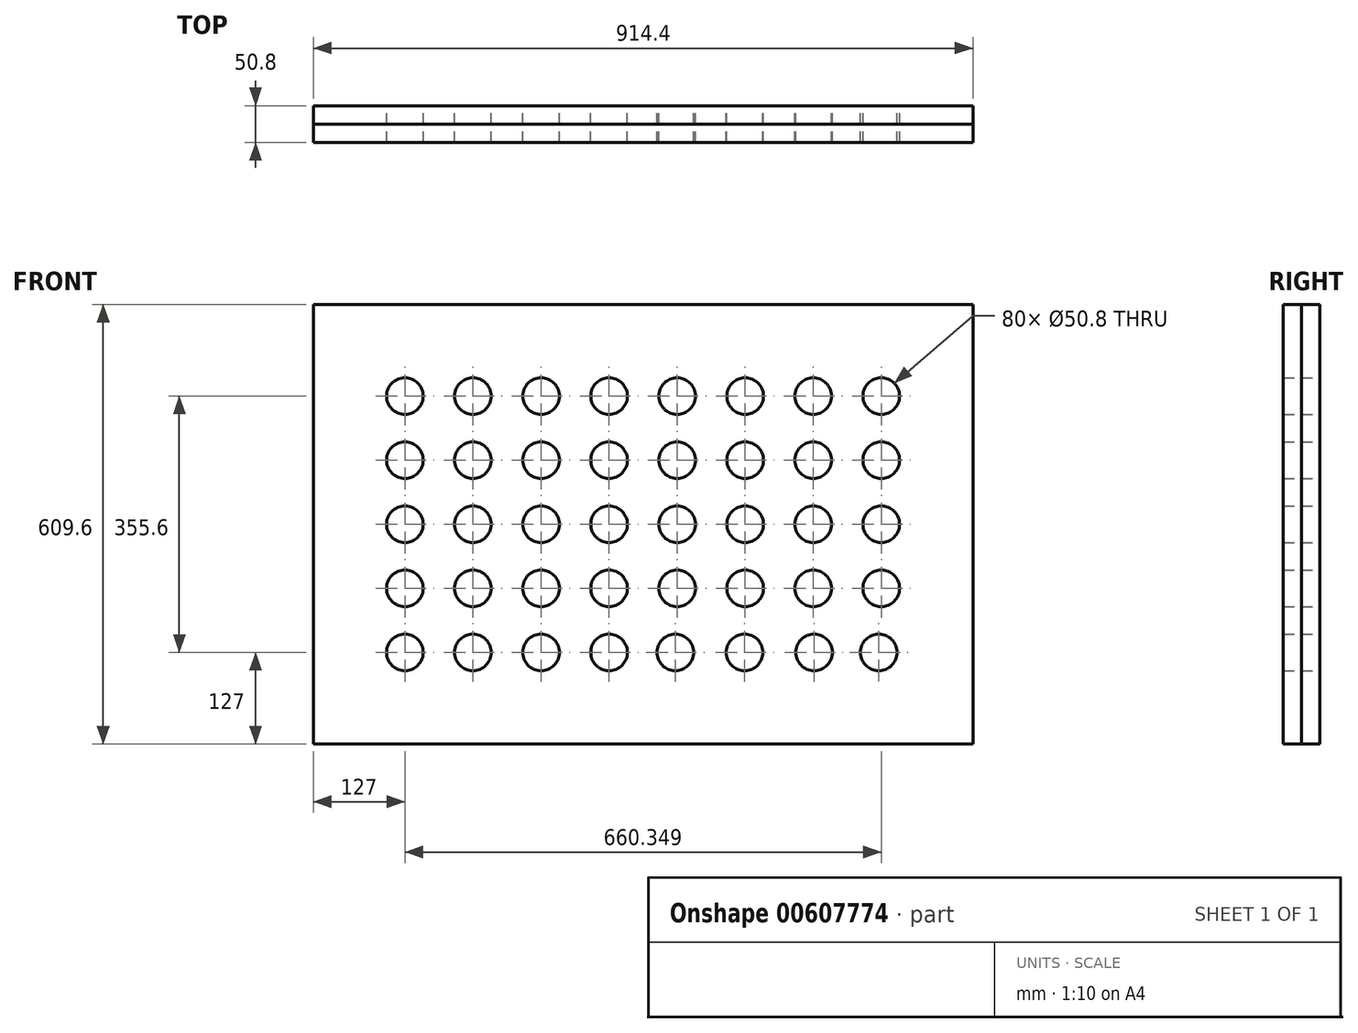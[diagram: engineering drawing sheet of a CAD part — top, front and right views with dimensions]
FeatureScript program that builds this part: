
annotation { "Feature Type Name" : "Feature", "Feature Type Description" : "" }
export const myFeature = defineFeature(function(context is Context, id is Id, definition is map)
    precondition{}
    {
        {
            var Q0;
            Q0=qCreatedBy(makeId("Front.planeOp"),FACE);
            var sketch = newSketch(context, id + "F0", { "sketchPlane" : qUnion([Q0])});
            skLineSegment(sketch, "E0.bottom", {"start": v(0, 0) * mm, "end": v(-914.4, 0) * mm});
            skLineSegment(sketch, "E0.top", {"start": v(0, 609.6) * mm, "end": v(-914.4, 609.6) * mm});
            skLineSegment(sketch, "E0.left", {"start": v(0, 0) * mm, "end": v(0, 609.6) * mm});
            skLineSegment(sketch, "E0.right", {"start": v(-914.4, 0) * mm, "end": v(-914.4, 609.6) * mm});
            skCircle(sketch, "E1", {"center": v(-787.4, 482.6) * mm, "radius": 25.4 * mm});
            skCircle(sketch, "E2", {"center": v(-787.4, 393.7) * mm, "radius": 25.4 * mm});
            skCircle(sketch, "E3", {"center": v(-787.4, 304.8) * mm, "radius": 25.4 * mm});
            skCircle(sketch, "E4", {"center": v(-787.4, 215.9) * mm, "radius": 25.4 * mm});
            skCircle(sketch, "E5", {"center": v(-787.4, 127) * mm, "radius": 25.4 * mm});
            skCircle(sketch, "E6", {"center": v(-693.06, 482.6) * mm, "radius": 25.4 * mm});
            skCircle(sketch, "E7", {"center": v(-598.73, 482.6) * mm, "radius": 25.4 * mm});
            skCircle(sketch, "E8", {"center": v(-504.4, 482.6) * mm, "radius": 25.4 * mm});
            skCircle(sketch, "E9", {"center": v(-410.06, 482.6) * mm, "radius": 25.4 * mm});
            skCircle(sketch, "E10", {"center": v(-315.72, 482.6) * mm, "radius": 25.4 * mm});
            skCircle(sketch, "E11", {"center": v(-221.39, 482.6) * mm, "radius": 25.4 * mm});
            skCircle(sketch, "E12", {"center": v(-127.05, 482.6) * mm, "radius": 25.4 * mm});
            skCircle(sketch, "E13", {"center": v(-693.06, 393.7) * mm, "radius": 25.4 * mm});
            skCircle(sketch, "E14", {"center": v(-598.73, 393.7) * mm, "radius": 25.4 * mm});
            skCircle(sketch, "E15", {"center": v(-504.4, 393.7) * mm, "radius": 25.4 * mm});
            skCircle(sketch, "E16", {"center": v(-410.06, 393.7) * mm, "radius": 25.4 * mm});
            skCircle(sketch, "E17", {"center": v(-315.72, 393.7) * mm, "radius": 25.4 * mm});
            skCircle(sketch, "E18", {"center": v(-221.39, 393.7) * mm, "radius": 25.4 * mm});
            skCircle(sketch, "E19", {"center": v(-127.05, 393.7) * mm, "radius": 25.4 * mm});
            skCircle(sketch, "E20", {"center": v(-693.06, 304.8) * mm, "radius": 25.4 * mm});
            skCircle(sketch, "E21", {"center": v(-598.73, 304.8) * mm, "radius": 25.4 * mm});
            skCircle(sketch, "E22", {"center": v(-504.4, 304.8) * mm, "radius": 25.4 * mm});
            skCircle(sketch, "E23", {"center": v(-410.06, 304.8) * mm, "radius": 25.4 * mm});
            skCircle(sketch, "E24", {"center": v(-315.72, 304.8) * mm, "radius": 25.4 * mm});
            skCircle(sketch, "E25", {"center": v(-221.39, 304.8) * mm, "radius": 25.4 * mm});
            skCircle(sketch, "E26", {"center": v(-127.05, 304.8) * mm, "radius": 25.4 * mm});
            skCircle(sketch, "E27", {"center": v(-693.06, 215.9) * mm, "radius": 25.4 * mm});
            skCircle(sketch, "E28", {"center": v(-598.73, 215.9) * mm, "radius": 25.4 * mm});
            skCircle(sketch, "E29", {"center": v(-504.4, 215.9) * mm, "radius": 25.4 * mm});
            skCircle(sketch, "E30", {"center": v(-410.06, 215.9) * mm, "radius": 25.4 * mm});
            skCircle(sketch, "E31", {"center": v(-315.72, 215.9) * mm, "radius": 25.4 * mm});
            skCircle(sketch, "E32", {"center": v(-221.39, 215.9) * mm, "radius": 25.4 * mm});
            skCircle(sketch, "E33", {"center": v(-127.05, 215.9) * mm, "radius": 25.4 * mm});
            skCircle(sketch, "E34", {"center": v(-693.06, 127) * mm, "radius": 25.4 * mm});
            skCircle(sketch, "E35", {"center": v(-598.73, 127) * mm, "radius": 25.4 * mm});
            skCircle(sketch, "E36", {"center": v(-504.4, 127) * mm, "radius": 25.4 * mm});
            skCircle(sketch, "E37", {"center": v(-412.6, 127.04) * mm, "radius": 25.4 * mm});
            skCircle(sketch, "E38", {"center": v(-316.44, 127) * mm, "radius": 25.4 * mm});
            skCircle(sketch, "E39", {"center": v(-220.22, 127) * mm, "radius": 25.4 * mm});
            skCircle(sketch, "E40", {"center": v(-130.5, 127.07) * mm, "radius": 25.4 * mm});
            skSolve(sketch);
        }
        {
            var Q0;
            Q0 = qSketchRegion(id + "F0", true);
            extrude(context, id + "F1", {"entities" : qUnion([Q0]), "depth" : 25.4 * mm, "offsetDistance" : 25.4 * mm});
        }
        {
            var Q0;
            Q0=makeQuery(id+"F1.opExtrude","CAP_FACE",FACE,{"disambiguationData":[OSD([sQuery(id+"F0.wireOp",EDGE,"E0.bottom"),sQuery(id+"F0.wireOp",EDGE,"E0.top"),sQuery(id+"F0.wireOp",EDGE,"E0.left"),sQuery(id+"F0.wireOp",EDGE,"E0.right"),sQuery(id+"F0.wireOp",EDGE,"E1"),sQuery(id+"F0.wireOp",EDGE,"9c005e61-8502-4910-8800-e6c45f4388ae"),sQuery(id+"F0.wireOp",EDGE,"E2"),sQuery(id+"F0.wireOp",EDGE,"E3"),sQuery(id+"F0.wireOp",EDGE,"E4"),sQuery(id+"F0.wireOp",EDGE,"E5")])],"isStart":false});
            extrude(context, id + "F2", {"entities" : qUnion([Q0]), "depth" : 25.4 * mm, "offsetDistance" : 25.4 * mm});
        }
    });
